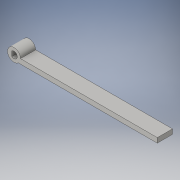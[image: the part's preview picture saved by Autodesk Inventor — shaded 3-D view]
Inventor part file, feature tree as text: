
AUTODESK INVENTOR PART (.ipt)
format: ipt  version: 2016 SP1 (Build 200210100, 210)  size: 99,840 bytes
history: native  units: in
note: dims shown in document units (in); Inventor stores cm internally (conversion verified against a paired STEP export)
features: extrude x1, sketch x1
ambient origin geometry x8: Origin, YZ Plane, XZ Plane, XY Plane, X Axis, Y Axis, Z Axis, Center Point
bodies: Solid1 (feature_tree)
feature tree (2):
  extrude  "Extrusion1"  Depth=0.37in
  sketch  "Sketch1"  dims[d0=0.1594in d2=0.315in d3=0.1319in d5=3.5in d7=0.117in d8=3.3425in d9=0.37in d10=0.0in]
